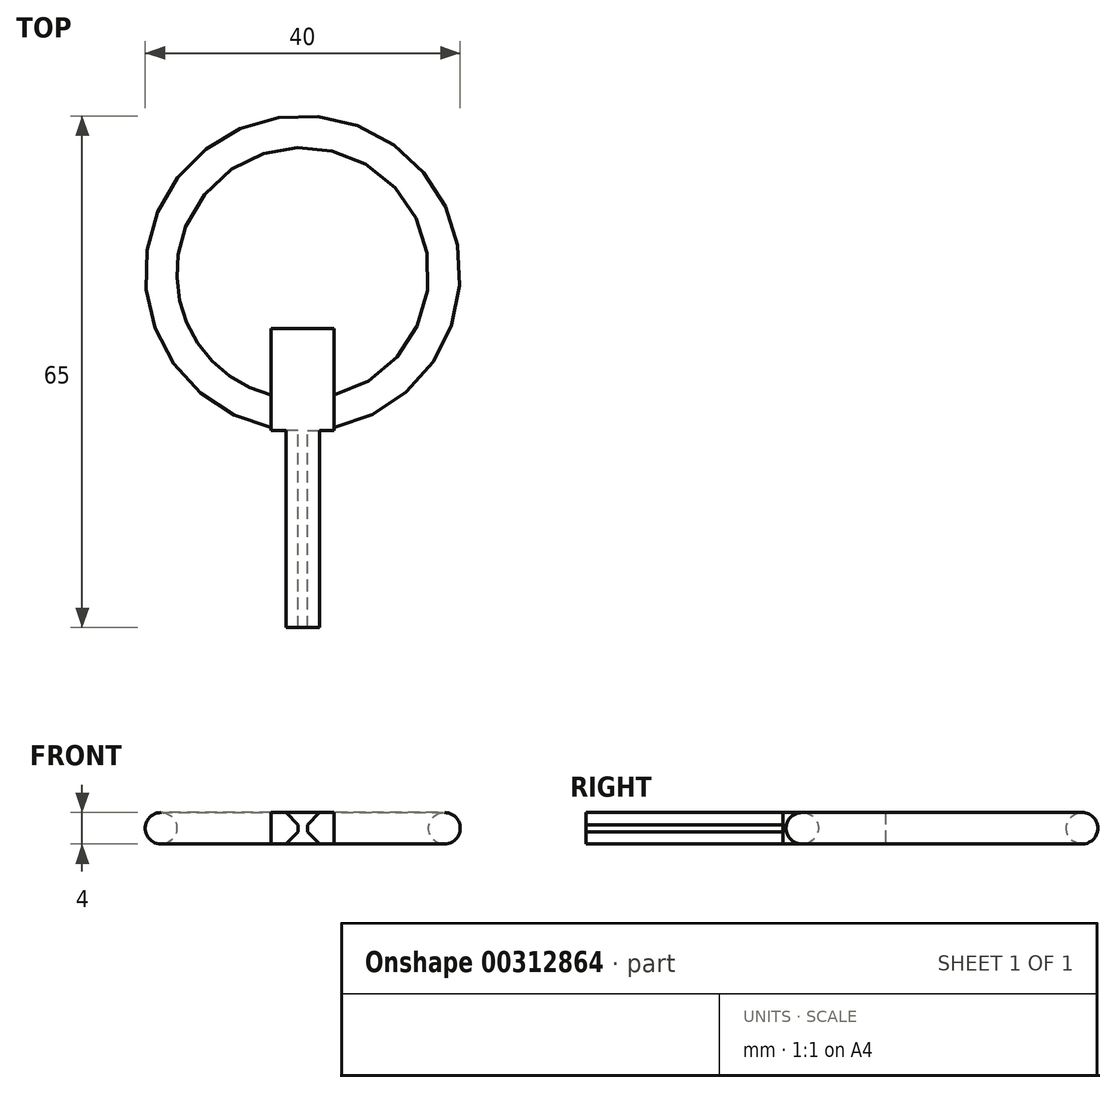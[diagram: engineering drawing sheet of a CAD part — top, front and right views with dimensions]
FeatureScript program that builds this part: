
annotation { "Feature Type Name" : "Feature", "Feature Type Description" : "" }
export const myFeature = defineFeature(function(context is Context, id is Id, definition is map)
    precondition{}
    {
        {
            var Q0;
            Q0=qCreatedBy(makeId("Front.planeOp"),FACE);
            var sketch = newSketch(context, id + "F0", { "sketchPlane" : qUnion([Q0])});
            skLineSegment(sketch, "E0", {"start": v(0, 0) * mm, "end": v(0, 22.5) * mm});
            skLineSegment(sketch, "E1", {"start": v(0, 0) * mm, "end": v(-18, 0) * mm});
            skCircle(sketch, "E2", {"center": v(-18, 0) * mm, "radius": 2 * mm});
            skSolve(sketch);
        }
        {
            var Q0;
            Q0=makeQuery(id+"F0.imprint","IMPRINT",FACE,{"disambiguationData":[TD([[makeQuery(id+"F0.imprint","IMPRINT",EDGE,{"derivedFrom":sQuery(id+"F0.wireOp",EDGE,"E2")}),1.0]])]});
            var Q1;
            Q1=sQuery(id+"F0.wireOp",EDGE,"E0");
            revolve(context, id + "F1", {"entities" : qUnion([Q0]), "axis" : qUnion([Q1]), "revolveType" : RevolveType.FULL});
        }
        {
            var Q0;
            Q0=qCreatedBy(makeId("Top.planeOp"),FACE);
            var sketch = newSketch(context, id + "F2", { "sketchPlane" : qUnion([Q0])});
            skLineSegment(sketch, "E3", {"start": v(0, 0) * mm, "end": v(0, -20) * mm});
            skLineSegment(sketch, "E4", {"start": v(0, -20) * mm, "end": v(4, -20) * mm});
            skLineSegment(sketch, "E5.bottom", {"start": v(4, -20) * mm, "end": v(-4, -20) * mm});
            skLineSegment(sketch, "E5.top", {"start": v(4, -7) * mm, "end": v(-4, -7) * mm});
            skLineSegment(sketch, "E5.left", {"start": v(4, -20) * mm, "end": v(4, -7) * mm});
            skLineSegment(sketch, "E5.right", {"start": v(-4, -20) * mm, "end": v(-4, -7) * mm});
            skSolve(sketch);
        }
        {
            var Q0;
            {var subQ5=sQuery(id+"F2.wireOp",EDGE,"E5.left");Q0=makeQuery(id+"F2.imprint","IMPRINT",FACE,{"disambiguationData":[TD([[makeQuery(id+"F2.imprint","IMPRINT",EDGE,{"derivedFrom":subQ5}),1.0]])]});}
            var Q1;
            {var subQ5=sQuery(id+"F2.wireOp",EDGE,"E5.right");Q1=makeQuery(id+"F2.imprint","IMPRINT",FACE,{"disambiguationData":[TD([[makeQuery(id+"F2.imprint","IMPRINT",EDGE,{"derivedFrom":subQ5}),-1.0]])]});}
            extrude(context, id + "F3", {"entities" : qUnion([Q0, Q1]), "operationType" : NewBodyOperationType.ADD, "endBound" : BoundingType.SYMMETRIC, "depth" : 4 * mm});
        }
        {
            var Q0;
            Q0=makeQuery(id+"F3.opExtrude","SWEPT_FACE",FACE,{"disambiguationData":[OSD([sQuery(id+"F2.wireOp",EDGE,"E5.bottom")])]});
            var sketch = newSketch(context, id + "F4", { "sketchPlane" : qUnion([Q0])});
            skLineSegment(sketch, "E6", {"start": v(4, 2) * mm, "end": v(0, 2) * mm});
            skLineSegment(sketch, "E7", {"start": v(0, 2) * mm, "end": v(-0.5, 2) * mm});
            skLineSegment(sketch, "E8", {"start": v(-0.5, 0.5) * mm, "end": v(-0.5, -0.5) * mm});
            skLineSegment(sketch, "E9", {"start": v(-0.5, -2) * mm, "end": v(0.5, -2) * mm});
            skLineSegment(sketch, "E10", {"start": v(0.5, -0.5) * mm, "end": v(0.5, 0.5) * mm});
            skLineSegment(sketch, "E11", {"start": v(0.5, 2) * mm, "end": v(0, 2) * mm});
            skLineSegment(sketch, "E12", {"start": v(0.5, 0.5) * mm, "end": v(2, 2) * mm});
            skLineSegment(sketch, "E13", {"start": v(-0.5, 0.5) * mm, "end": v(-2, 2) * mm});
            skLineSegment(sketch, "E14", {"start": v(0.5, -0.5) * mm, "end": v(2, -2) * mm});
            skLineSegment(sketch, "E15", {"start": v(-0.5, -0.5) * mm, "end": v(-2, -2) * mm});
            skLineSegment(sketch, "E16", {"start": v(-2, -2) * mm, "end": v(2, -2) * mm});
            skLineSegment(sketch, "E17", {"start": v(2, 2) * mm, "end": v(-2, 2) * mm});
            skLineSegment(sketch, "E18.0", {"start": v(0.6, -0.46) * mm, "end": v(2.07, -1.93) * mm});
            skLineSegment(sketch, "E18.1", {"start": v(0.6, -0.46) * mm, "end": v(0.6, 0.46) * mm});
            skLineSegment(sketch, "E18.2", {"start": v(0.6, 0.46) * mm, "end": v(2.07, 1.93) * mm});
            skLineSegment(sketch, "E19.0", {"start": v(-0.6, -0.46) * mm, "end": v(-2.07, -1.93) * mm});
            skLineSegment(sketch, "E19.1", {"start": v(-0.6, 0.46) * mm, "end": v(-0.6, -0.46) * mm});
            skLineSegment(sketch, "E19.2", {"start": v(-0.6, 0.46) * mm, "end": v(-2.07, 1.93) * mm});
            skLineSegment(sketch, "E20", {"start": v(-2.07, -1.93) * mm, "end": v(-2.14, -2) * mm});
            skLineSegment(sketch, "E21", {"start": v(-2.14, -2) * mm, "end": v(-2, -2) * mm});
            skLineSegment(sketch, "E22", {"start": v(2.07, -1.93) * mm, "end": v(2.14, -2) * mm});
            skLineSegment(sketch, "E23", {"start": v(2.14, -2) * mm, "end": v(2, -2) * mm});
            skLineSegment(sketch, "E24", {"start": v(-2.07, 1.93) * mm, "end": v(-2.14, 2) * mm});
            skLineSegment(sketch, "E25", {"start": v(2.07, 1.93) * mm, "end": v(2.14, 2) * mm});
            skSolve(sketch);
        }
        {
            var Q0;
            Q0=makeQuery(id+"F4.imprint","IMPRINT",FACE,{"disambiguationData":[TD([[makeQuery(id+"F4.imprint","IMPRINT",EDGE,{"derivedFrom":sQuery(id+"F4.wireOp",EDGE,"E8")}),1.0]])]});
            var Q1;
            Q1=makeQuery(id+"F4.imprint","IMPRINT",FACE,{"disambiguationData":[TD([[makeQuery(id+"F4.imprint","IMPRINT",EDGE,{"derivedFrom":sQuery(id+"F4.wireOp",EDGE,"E10")}),-1.0]])]});
            var Q2;
            Q2=makeQuery(id+"F4.imprint","IMPRINT",FACE,{"disambiguationData":[TD([[makeQuery(id+"F4.imprint","IMPRINT",EDGE,{"derivedFrom":sQuery(id+"F4.wireOp",EDGE,"E8")}),-1.0]])]});
            extrude(context, id + "F5", {"entities" : qUnion([Q0, Q1, Q2]), "operationType" : NewBodyOperationType.ADD, "depth" : 25 * mm});
        }
    });
